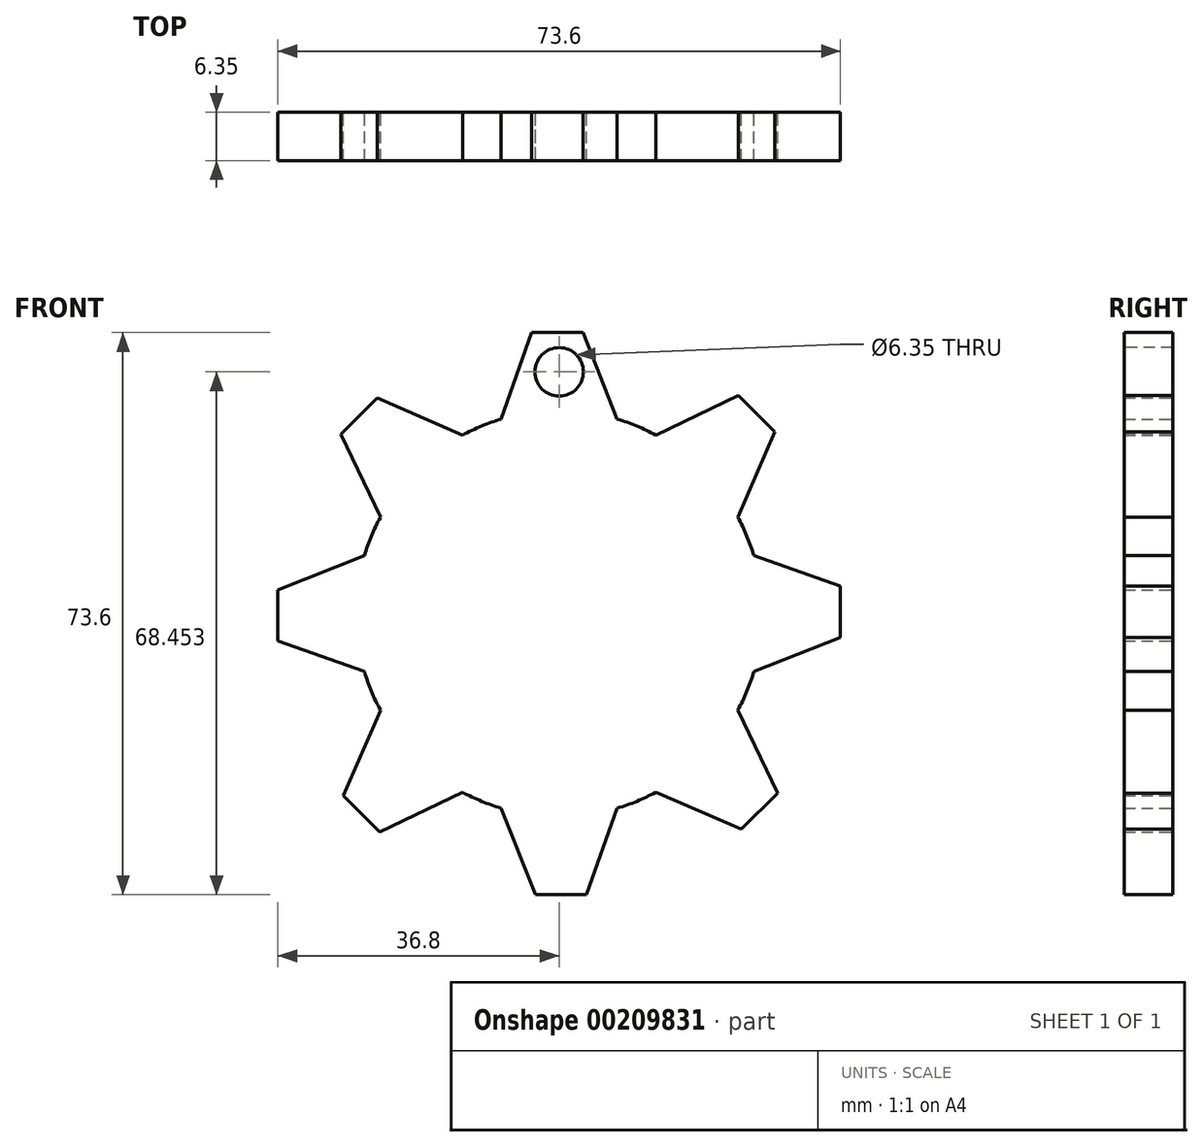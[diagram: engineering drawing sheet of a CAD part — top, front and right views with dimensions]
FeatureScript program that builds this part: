
annotation { "Feature Type Name" : "Feature", "Feature Type Description" : "" }
export const myFeature = defineFeature(function(context is Context, id is Id, definition is map)
    precondition{}
    {
        {
            var Q0;
            Q0=qCreatedBy(makeId("Front.planeOp"),FACE);
            var sketch = newSketch(context, id + "F0", { "sketchPlane" : qUnion([Q0])});
            skCircle(sketch, "E0", {"center": v(0, 0) * mm, "radius": 38.1 * mm});
            skSolve(sketch);
        }
        {
            var Q0;
            Q0 = qSketchRegion(id + "F0", true);
            extrude(context, id + "F1", {"entities" : qUnion([Q0]), "depth" : 6.35 * mm});
        }
        {
            var Q0;
            Q0=makeQuery(id+"F1.opExtrude","CAP_FACE",FACE,{"disambiguationData":[OSD([sQuery(id+"F0.wireOp",EDGE,"E0")])],"isStart":false});
            var sketch = newSketch(context, id + "F2", { "sketchPlane" : qUnion([Q0])});
            skCircle(sketch, "E1", {"center": v(0, 31.65) * mm, "radius": 3.18 * mm});
            skSolve(sketch);
        }
        {
            var Q0;
            Q0 = qSketchRegion(id + "F2", true);
            extrude(context, id + "F3", {"entities" : qUnion([Q0]), "operationType" : NewBodyOperationType.REMOVE, "endBound" : BoundingType.THROUGH_ALL, "oppositeDirection" : true, "depth" : 25.4 * mm});
        }
        {
            var Q0;
            Q0=qCreatedBy(makeId("Front.planeOp"),FACE);
            var sketch = newSketch(context, id + "F4", { "sketchPlane" : qUnion([Q0])});
            skLineSegment(sketch, "E2", {"start": v(-3.6, 36.8) * mm, "end": v(3.1, 36.8) * mm});
            skLineSegment(sketch, "E3", {"start": v(3.1, 36.8) * mm, "end": v(7.62, 25.4) * mm});
            skLineSegment(sketch, "E4", {"start": v(-3.6, 36.8) * mm, "end": v(-7.62, 25.4) * mm});
            skLineSegment(sketch, "E5.1.0", {"start": v(-28.56, 23.48) * mm, "end": v(-23.35, 12.57) * mm});
            skLineSegment(sketch, "E5.1.1", {"start": v(-23.82, 28.22) * mm, "end": v(-12.57, 23.35) * mm});
            skLineSegment(sketch, "E5.1.2", {"start": v(-28.56, 23.48) * mm, "end": v(-23.82, 28.22) * mm});
            skLineSegment(sketch, "E5.2.0", {"start": v(-36.8, -3.6) * mm, "end": v(-25.4, -7.62) * mm});
            skLineSegment(sketch, "E5.2.1", {"start": v(-36.8, 3.1) * mm, "end": v(-25.4, 7.62) * mm});
            skLineSegment(sketch, "E5.2.2", {"start": v(-36.8, -3.6) * mm, "end": v(-36.8, 3.1) * mm});
            skLineSegment(sketch, "E5.3.0", {"start": v(-23.48, -28.56) * mm, "end": v(-12.57, -23.35) * mm});
            skLineSegment(sketch, "E5.3.1", {"start": v(-28.22, -23.82) * mm, "end": v(-23.35, -12.57) * mm});
            skLineSegment(sketch, "E5.3.2", {"start": v(-23.48, -28.56) * mm, "end": v(-28.22, -23.82) * mm});
            skLineSegment(sketch, "E5.4.0", {"start": v(3.6, -36.8) * mm, "end": v(7.62, -25.4) * mm});
            skLineSegment(sketch, "E5.4.1", {"start": v(-3.1, -36.8) * mm, "end": v(-7.62, -25.4) * mm});
            skLineSegment(sketch, "E5.4.2", {"start": v(3.6, -36.8) * mm, "end": v(-3.1, -36.8) * mm});
            skLineSegment(sketch, "E5.5.0", {"start": v(28.56, -23.48) * mm, "end": v(23.35, -12.57) * mm});
            skLineSegment(sketch, "E5.5.1", {"start": v(23.82, -28.22) * mm, "end": v(12.57, -23.35) * mm});
            skLineSegment(sketch, "E5.5.2", {"start": v(28.56, -23.48) * mm, "end": v(23.82, -28.22) * mm});
            skLineSegment(sketch, "E5.6.0", {"start": v(36.8, 3.6) * mm, "end": v(25.4, 7.62) * mm});
            skLineSegment(sketch, "E5.6.1", {"start": v(36.8, -3.1) * mm, "end": v(25.4, -7.62) * mm});
            skLineSegment(sketch, "E5.6.2", {"start": v(36.8, 3.6) * mm, "end": v(36.8, -3.1) * mm});
            skLineSegment(sketch, "E5.7.0", {"start": v(23.48, 28.56) * mm, "end": v(12.57, 23.35) * mm});
            skLineSegment(sketch, "E5.7.1", {"start": v(28.22, 23.82) * mm, "end": v(23.35, 12.57) * mm});
            skLineSegment(sketch, "E5.7.2", {"start": v(23.48, 28.56) * mm, "end": v(28.22, 23.82) * mm});
            skPoint(sketch, "E5.center", {"position": v(0, 0) * mm});
            skArc(sketch, "E6", {"start": v(-7.6, 25.47) * mm, "mid": v(-10.17, 24.55) * mm, "end": v(-12.64, 23.38) * mm});
            skArc(sketch, "E7.trimOffspring", {"start": v(12.64, 23.38) * mm, "mid": v(10.17, 24.56) * mm, "end": v(7.6, 25.47) * mm});
            skArc(sketch, "E8.trimOffspring", {"start": v(-23.38, 12.64) * mm, "mid": v(-24.56, 10.17) * mm, "end": v(-25.47, 7.6) * mm});
            skArc(sketch, "E9.trimOffspring", {"start": v(-25.47, -7.6) * mm, "mid": v(-24.55, -10.17) * mm, "end": v(-23.38, -12.64) * mm});
            skArc(sketch, "E10.trimOffspring", {"start": v(-12.64, -23.38) * mm, "mid": v(-10.17, -24.56) * mm, "end": v(-7.6, -25.47) * mm});
            skArc(sketch, "E11.trimOffspring", {"start": v(7.6, -25.47) * mm, "mid": v(10.17, -24.55) * mm, "end": v(12.64, -23.38) * mm});
            skArc(sketch, "E12.trimOffspring", {"start": v(23.38, -12.64) * mm, "mid": v(24.56, -10.17) * mm, "end": v(25.47, -7.6) * mm});
            skArc(sketch, "E13.trimOffspring", {"start": v(25.47, 7.6) * mm, "mid": v(24.55, 10.17) * mm, "end": v(23.38, 12.64) * mm});
            skSolve(sketch);
        }
        {
            var Q0;
            Q0 = qSketchRegion(id + "F4", true);
            extrude(context, id + "F5", {"entities" : qUnion([Q0]), "operationType" : NewBodyOperationType.INTERSECT, "depth" : 25.4 * mm});
        }
    });
